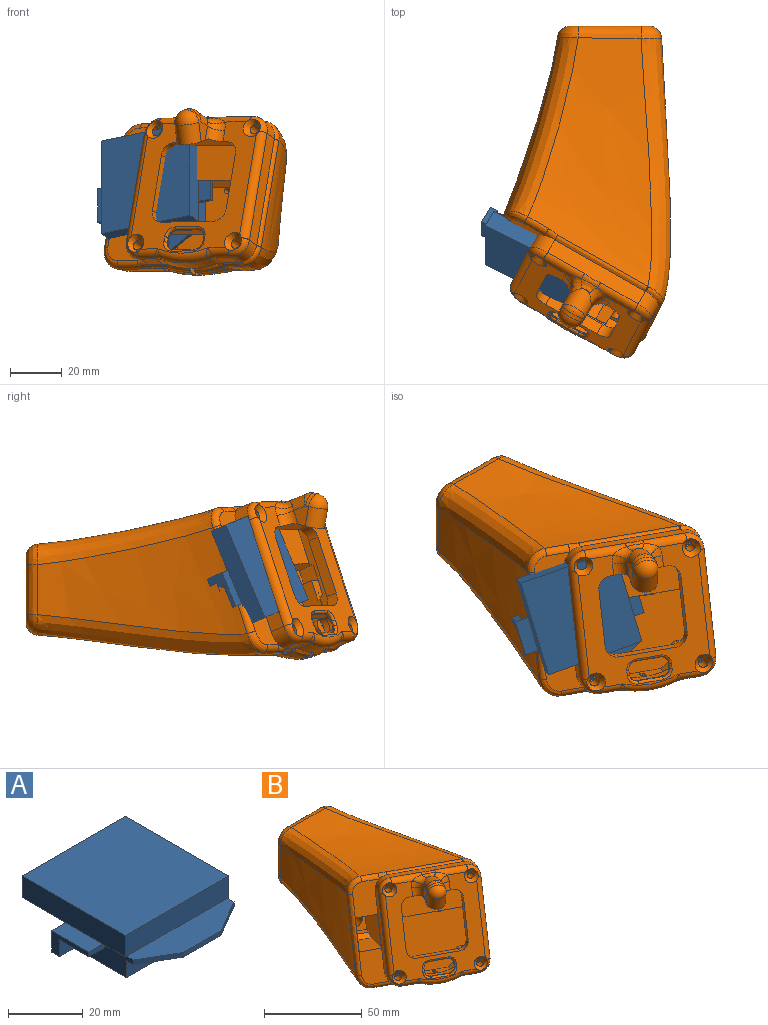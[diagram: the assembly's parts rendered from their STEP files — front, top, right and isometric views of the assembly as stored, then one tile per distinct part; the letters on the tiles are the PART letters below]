
ASSEMBLY  parts=2 mates=1
PART A: 32 faces, bbox 49.5x48.5x14 mm
  f0: plane 14x7mm, normal (-1,0,0), area 37.5mm2, adj f1,f7,f10,f13,f30,f31
  f1: plane 5.75x1.5mm, normal (0,-1,0), area 8.6mm2, adj f0,f11,f13,f14,f31
  f2: plane 5.75x1.5mm, normal (0,-1,0), area 8.6mm2, adj f3,f8,f12,f15,f29
  f3: plane 14x7mm, normal (1,0,0), area 37.5mm2, adj f2,f7,f8,f10,f28,f29
  f4: plane 12x7mm, normal (-0.5,-0.86,0), area 20.8mm2, adj f5,f9,f11,f27
  f5: plane 14x1.5mm, normal (0,-1,0), area 21mm2, adj f4,f6,f9,f27
  f6: plane 12x7mm, normal (0.5,-0.86,0), area 20.8mm2, adj f5,f9,f12,f27
  f7: plane 49.5x22.5mm, normal (0,0,-1), area 802.5mm2, adj f0,f3,f10,f11,f12,f22,f23,f24
  f8: plane 14x5.25mm, normal (0,0,1), area 73.5mm2, adj f2,f3,f10,f19
  f9: plane 38x9.5mm, normal (0,0,1), area 277mm2, adj f4,f5,f6,f11,f12,f18
  f10: plane 49.5x7mm, normal (0,1,0), area 107.3mm2, adj f0,f3,f7,f8,f13,f21,f22,f23
  f11: plane 22x7mm, normal (-1,0,0), area 123.8mm2, adj f1,f4,f7,f9,f14,f26,f27,f30
  f12: plane 22x7mm, normal (1,0,0), area 123.8mm2, adj f2,f6,f7,f9,f15,f26,f27,f28
  f13: plane 14x5.25mm, normal (0,0,1), area 73.5mm2, adj f0,f1,f10,f17
  f14: plane 8.5x0.5mm, normal (0,0,-1), area 4.2mm2, adj f1,f11,f17,f18
  f15: plane 8.5x0.5mm, normal (0,0,-1), area 4.3mm2, adj f2,f12,f18,f19
  f16: plane 39x7mm, normal (0,1,0), area 273mm2, adj f17,f19,f20,f21
  f17: plane 39x7mm, normal (-1,0,0), area 273mm2, adj f13,f14,f16,f18,f20,f21
  f18: plane 39x7mm, normal (0,-1,0), area 273mm2, adj f9,f14,f15,f17,f19,f20
  f19: plane 39x7mm, normal (1,0,0), area 273mm2, adj f8,f15,f16,f18,f20,f21
  f20: plane 39x39mm, normal (0,0,1), area 1521mm2, adj f16,f17,f18,f19
  f21: plane 39x16.5mm, normal (0,0,-1), area 643.5mm2, adj f10,f16,f17,f19
  f22: plane 5.5x2mm, normal (1,0,0), area 11mm2, adj f7,f10,f24,f25
  f23: plane 5.5x2mm, normal (-1,0,0), area 11mm2, adj f7,f10,f24,f25
  f24: plane 43.5x5.5mm, normal (0,1,0), area 239.2mm2, adj f7,f22,f23,f25
  f25: plane 43.5x2mm, normal (0,0,-1), area 87mm2, adj f10,f22,f23,f24
  f26: plane 38x5.5mm, normal (0,-1,0), area 209mm2, adj f7,f11,f12,f27
  f27: plane 38x9.5mm, normal (0,0,-1), area 277mm2, adj f4,f5,f6,f11,f12,f26
  f28: plane 5.75x5.5mm, normal (0,-1,0), area 31.6mm2, adj f3,f7,f12,f29
  f29: plane 11x5.75mm, normal (0,0,-1), area 63.2mm2, adj f2,f3,f12,f28
  f30: plane 5.75x5.5mm, normal (0,-1,0), area 31.6mm2, adj f0,f7,f11,f31
  f31: plane 11x5.75mm, normal (0,0,-1), area 63.2mm2, adj f0,f1,f11,f30
PART B: 314 faces, bbox 89.2x132.2x70.9 mm
  f0: cylinder r=2.3mm len=4.98mm, axis (-0.12,-0.17,0.98), area 36.2mm2, adj f1,f102,f306,f307
  f1: torus R=3mm, axis (-0.87,0.49,-0.02), area 47.5mm2, adj f0,f105,f308,f309
  f2: plane 39.21x38.23mm, normal (0.47,0.81,-0.34), area 1463.8mm2, adj f129,f130,f151,f152,f153,f154,f278,f279
  f3: plane 1.48x1.13mm, normal (0.47,0.81,-0.34), area 0.5mm2, adj f12,f96,f289
  f4: plane 1.62x0.92mm, normal (0.47,0.81,-0.34), area 0.5mm2, adj f12,f39,f288
  f5: plane 1.88x1.74mm, normal (0.47,0.81,-0.34), area 0.9mm2, adj f38,f39,f295
  f6: plane 2.05x1.91mm, normal (0.47,0.81,-0.34), area 0.9mm2, adj f38,f96,f297
  f7: plane 1.62x0.92mm, normal (0.47,0.81,-0.34), area 0.5mm2, adj f11,f96,f292
  f8: plane 1.88x1.74mm, normal (0.47,0.81,-0.34), area 0.9mm2, adj f36,f96,f300
  f9: plane 2.05x1.91mm, normal (0.47,0.81,-0.34), area 0.9mm2, adj f36,f37,f302
  f10: plane 1.48x1.13mm, normal (0.47,0.81,-0.34), area 0.5mm2, adj f11,f37,f291
  f11: plane 37.28x15.33mm, normal (-0.87,0.49,-0.02), area 156mm2, adj f7,f10,f14,f94,f98,f99,f100,f291
  f12: plane 37.28x15.33mm, normal (0.87,-0.49,0.02), area 156mm2, adj f3,f4,f14,f94,f97,f99,f100,f288
  f13: plane 34.01x20.01mm, normal (0.47,0.81,-0.34), area 67.8mm2, adj f14,f40,f41,f42,f43,f95,f164,f241
  f14: plane 36.22x23.14mm, normal (0.16,0.3,0.94), area 102.7mm2, adj f11,f12,f13,f15,f94,f97,f98,f266
  f15: plane 25.65x15.22mm, normal (0.47,0.81,-0.34), area 55.8mm2, adj f14,f248,f263,f264,f265,f266,f267,f268
  f16: plane 2.37x1.14mm, normal (-0.47,-0.81,0.34), area 0.3mm2, adj f244,f245,f264
  f17: plane 2.2x1.46mm, normal (-0.47,-0.81,0.34), area 0.3mm2, adj f244,f249,f264
  f18: plane 8.05x7.05mm, normal (0.47,0.81,-0.34), area 34.6mm2, adj f248,f249,f250,f251,f264,f265
  f19: plane 7.15x7.09mm, normal (0.47,0.81,-0.34), area 34.6mm2, adj f245,f246,f247,f248,f263,f264
  f20: cylinder r=40mm len=12.67mm, axis (-0.47,-0.81,0.34), area 31.5mm2, adj f21,f181,f182,f242
  f21: bspline ~10.64x5.97mm, area 26.4mm2, adj f20,f164,f196,f242,f274
  f22: cone r=0mm half-angle=59deg, axis (-0.47,-0.81,0.34), area 6.8mm2, adj f177,f240
  f23: cone r=0mm half-angle=59deg, axis (-0.47,-0.81,0.34), area 6.8mm2, adj f175,f238
  f24: cone r=0mm half-angle=59deg, axis (-0.47,-0.81,0.34), area 6.8mm2, adj f173,f236
  f25: cone r=0mm half-angle=59deg, axis (-0.47,-0.81,0.34), area 6.8mm2, adj f171,f234
  f26: plane 51.05x48.58mm, normal (-0.47,-0.81,0.34), area 1023.4mm2, adj f27,f28,f29,f30,f31,f32,f90,f91
  f27: cylinder r=3mm len=42.42mm, axis (0.16,0.3,0.94), area 206.1mm2, adj f26,f86,f165,f167,f172,f178
  f28: cylinder r=3mm len=16.24mm, axis (0.87,-0.49,0.02), area 70.2mm2, adj f26,f89,f167,f169,f178,f228
  f29: cylinder r=3mm len=42.32mm, axis (-0.16,-0.3,-0.94), area 206.1mm2, adj f26,f88,f168,f170,f174,f176
  f30: cylinder r=3mm len=16.5mm, axis (0.87,-0.49,0.02), area 71.6mm2, adj f26,f89,f169,f170,f176,f230
  f31: cylinder r=3mm len=9.07mm, axis (-0.87,0.49,-0.02), area 38mm2, adj f26,f33,f168,f174,f275
  f32: cylinder r=3mm len=8.81mm, axis (-0.87,0.49,-0.02), area 36.6mm2, adj f26,f87,f165,f172,f277
  f33: plane 9.02x8.41mm, normal (-0.16,-0.3,-0.94), area 42.8mm2, adj f31,f156,f190,f192,f194,f274
  f34: plane 51.68x22.7mm, normal (-0.47,-0.81,0.34), area 442.6mm2, adj f44,f46,f47,f48,f86,f155,f158,f199
  f35: plane 44.3x31.36mm, normal (-0.47,-0.81,0.34), area 1192.8mm2, adj f36,f38,f40,f41,f42,f43,f95,f96
  f36: plane 14.13x10.96mm, normal (-0.87,0.49,-0.02), area 62.4mm2, adj f8,f9,f35,f37,f96,f148,f149,f301
  f37: plane 5.43x3.75mm, normal (0.16,0.3,0.94), area 6.7mm2, adj f9,f10,f36,f41,f98,f149,f303
  f38: plane 14.13x10.96mm, normal (0.87,-0.49,0.02), area 62.4mm2, adj f5,f6,f35,f39,f96,f143,f145,f296
  f39: plane 5.43x3.75mm, normal (0.16,0.3,0.94), area 6.7mm2, adj f4,f5,f38,f43,f97,f145,f294
  f40: plane 11.47x9.97mm, normal (-0.33,0.52,0.79), area 67.8mm2, adj f13,f35,f41,f95,f137,f141
  f41: plane 18.04x12.36mm, normal (-0.87,0.49,-0.02), area 123.4mm2, adj f13,f35,f37,f40,f98,f138,f141,f148
  f42: plane 12.49x10.94mm, normal (0.59,0,0.81), area 67.8mm2, adj f13,f35,f43,f95,f131,f135
  f43: plane 18.04x12.36mm, normal (0.87,-0.49,0.02), area 123.4mm2, adj f13,f35,f39,f42,f97,f133,f135,f143
  f44: plane 23.33x20.35mm, normal (0.16,0.3,0.94), area 253.7mm2, adj f34,f46,f47,f127
  f45: plane 12.88x12.36mm, normal (-0.47,-0.81,0.34), area 95.7mm2, adj f46,f47,f111,f125,f128
  f46: plane 29.25x25.15mm, normal (0.87,-0.49,0.02), area 513.1mm2, adj f34,f44,f45,f48,f125,f126,f127,f128
  f47: plane 29.25x25.15mm, normal (-0.87,0.49,-0.02), area 513.1mm2, adj f34,f44,f45,f48,f125,f126,f127,f128
  f48: plane 23.33x20.35mm, normal (-0.16,-0.3,-0.94), area 253.7mm2, adj f34,f46,f47,f126
  f49: plane 11x8.5mm, normal (0,1,0), area 39.4mm2, adj f50,f82,f84,f123,f124
  f50: cylinder r=4.15mm len=8.3mm, axis (0,1,0), area 109.3mm2, adj f49,f55,f313
  f51: plane 32.12x2.88mm, normal (0.57,0,0.82), area 106.5mm2, adj f53,f57,f115,f284,f312
  f52: plane 39.5x39.45mm, normal (0,0,-1), area 982.6mm2, adj f53,f56,f58,f116,f122,f278,f280,f287
  f53: plane 30.04x6.13mm, normal (1,0,0), area 172.5mm2, adj f51,f52,f280,f282,f284,f312
  f54: bspline ~46.34x45.04mm, area 1291.2mm2, adj f55,f116,f119,f120,f279,f287,f304
  f55: plane 17.61x17.4mm, normal (-0.17,-0.98,0), area 253.1mm2, adj f50,f54,f115,f117,f313
  f56: bspline ~30x26.65mm, area 34.9mm2, adj f52,f58,f278,f285
  f57: bspline ~44.17x31.12mm, area 519.2mm2, adj f51,f114,f115,f117,f118,f281,f283,f284
  f58: bspline ~40.13x38.49mm, area 722mm2, adj f52,f56,f285,f287
  f59: plane 7.87x5.82mm, normal (-0.87,0.49,-0.02), area 34.1mm2, adj f102,f106,f108,f110,f226
  f60: plane 30.55x25.51mm, normal (0,1,0), area 353.1mm2, adj f74,f75,f179,f208,f209,f210,f211,f212
  f61: bspline ~124.98x70.78mm, area 3534.6mm2, adj f160,f161,f180,f182,f183,f184,f185,f192
  f62: plane 18.13x15.13mm, normal (0,0,1), area 239.7mm2, adj f69,f72,f73,f74,f75,f76,f179,f220
  f63: bspline ~90.35x62.26mm, area 2378.1mm2, adj f161,f162,f203,f214
  f64: bspline ~124.98x63.62mm, area 3405.4mm2, adj f159,f160,f187,f189,f210
  f65: bspline ~106.69x69.6mm, area 3144.9mm2, adj f159,f162,f195,f197,f199,f212
  f66: plane 18.04x10.34mm, normal (1,0,0), area 185.4mm2, adj f69,f70,f73,f179
  f67: plane 18.02x15.02mm, normal (0,0,-1), area 270mm2, adj f69,f70,f71,f179
  f68: plane 18.04x10.34mm, normal (-1,0,0), area 185.4mm2, adj f69,f71,f72,f179
  f69: plane 29x24.3mm, normal (0,1,0), area 596.6mm2, adj f62,f66,f67,f68,f70,f71,f72,f73
  f70: cylinder r=7mm len=18mm, axis (0,1,0), area 197.9mm2, adj f66,f67,f69,f179
  f71: cylinder r=7mm len=18mm, axis (0,-1,0), area 197.9mm2, adj f67,f68,f69,f179
  f72: cylinder r=7mm len=18mm, axis (0,1,0), area 197.9mm2, adj f62,f68,f69,f179
  f73: cylinder r=7mm len=18mm, axis (0,-1,0), area 197.9mm2, adj f62,f66,f69,f179
  f74: plane 10.05x5.77mm, normal (-1,0,0), area 37.3mm2, adj f60,f62,f179,f208,f219,f220
  f75: plane 10.14x5.93mm, normal (1,0,0), area 37.6mm2, adj f60,f62,f179,f216,f217,f223
  f76: plane 3.34x0.54mm, normal (0,1,0), area 1.7mm2, adj f62,f218,f220,f221,f223,f224
  f77: plane 12.7x2.8mm, normal (0,0,-1), area 35.6mm2, adj f69,f78,f80,f81
  f78: plane 5.2x2.8mm, normal (1,0,0), area 14.6mm2, adj f69,f77,f79,f81
  f79: plane 12.7x2.8mm, normal (0,0,1), area 35.6mm2, adj f69,f78,f80,f81
  f80: plane 5.2x2.8mm, normal (-1,0,0), area 14.6mm2, adj f69,f77,f79,f81
  f81: plane 16x8.5mm, normal (0,-1,0), area 70mm2, adj f77,f78,f79,f80,f82,f83,f84,f85
  f82: plane 29.7x16mm, normal (0,0,1), area 454.7mm2, adj f49,f81,f83,f85,f123,f124
  f83: plane 21.5x8.5mm, normal (-1,0,0), area 182.8mm2, adj f81,f82,f84,f124
  f84: plane 29.7x16mm, normal (0,0,-1), area 454.7mm2, adj f49,f81,f83,f85,f123,f124
  f85: plane 21.5x8.5mm, normal (1,0,0), area 182.8mm2, adj f81,f82,f84,f123
  f86: plane 43.39x18.3mm, normal (-0.87,0.49,-0.02), area 264mm2, adj f27,f34,f155,f158
  f87: plane 8.76x8.26mm, normal (-0.16,-0.3,-0.94), area 41mm2, adj f32,f155,f202,f204,f276
  f88: plane 43.39x18.3mm, normal (0.87,-0.49,0.02), area 264mm2, adj f29,f156,f157,f186,f187
  f89: plane 38.01x24.92mm, normal (0.16,0.3,0.94), area 244.4mm2, adj f28,f30,f157,f158,f169,f193,f195
  f90: plane 23.11x10.59mm, normal (-0.87,0.49,-0.02), area 101.2mm2, adj f26,f94,f269,f272
  f91: plane 22.05x14.96mm, normal (0.16,0.3,0.94), area 101.2mm2, adj f26,f94,f269,f270
  f92: plane 23.11x10.59mm, normal (0.87,-0.49,0.02), area 101.2mm2, adj f26,f94,f270,f271
  f93: plane 22.05x14.96mm, normal (-0.16,-0.3,-0.94), area 143.5mm2, adj f26,f94,f102,f226,f232,f271,f272
  f94: plane 39.98x36.35mm, normal (0.47,0.81,-0.34), area 422.1mm2, adj f11,f12,f14,f90,f91,f92,f93,f100
  f95: plane 17.66x14.43mm, normal (0.16,0.3,0.94), area 116.2mm2, adj f13,f35,f40,f42,f241,f242,f243,f260
  f96: plane 47.03x31.15mm, normal (-0.16,-0.3,-0.94), area 398.4mm2, adj f3,f6,f7,f8,f35,f36,f38,f99
  f97: plane 7.71x2.65mm, normal (-0.47,-0.81,0.34), area 2.5mm2, adj f12,f14,f39,f43
  f98: plane 7.71x2.65mm, normal (-0.47,-0.81,0.34), area 2.5mm2, adj f11,f14,f37,f41
  f99: plane 36.43x24.03mm, normal (-0.47,-0.81,0.34), area 595.8mm2, adj f11,f12,f96,f100
  f100: plane 36.22x23.14mm, normal (-0.16,-0.3,-0.94), area 180.3mm2, adj f11,f12,f94,f99
  f101: plane 7.87x5.82mm, normal (0.87,-0.49,0.02), area 34.1mm2, adj f102,f106,f108,f110,f232
  f102: plane 12.21x12.17mm, normal (0.12,0.17,-0.98), area 74.9mm2, adj f0,f59,f93,f101,f110,f226,f232,f306
  f103: cylinder r=2.3mm len=6.68mm, axis (0.47,0.81,-0.34), area 71.2mm2, adj f104,f129
  f104: cylinder r=2.3mm len=8.33mm, axis (0.49,0.87,-0.07), area 95.7mm2, adj f103,f105
  f105: cylinder r=2.3mm len=7.01mm, axis (0.47,0.81,-0.34), area 72mm2, adj f1,f104,f310
  f106: cylinder r=5mm len=12.56mm, axis (-0.47,-0.81,0.34), area 107.4mm2, adj f59,f101,f107,f227,f228,f229,f230,f231
  f107: sphere r=5mm, area 27.9mm2, adj f106,f108
  f108: cylinder r=5mm len=9.46mm, axis (-0.48,-0.85,-0.21), area 23.8mm2, adj f59,f101,f107,f109
  f109: sphere r=5mm, area 314.2mm2, adj f108,f110
  f110: cylinder r=5mm len=10.21mm, axis (0.12,0.17,-0.98), area 121.3mm2, adj f59,f101,f102,f109
  f111: cylinder r=4.5mm len=15mm, axis (-0.47,-0.81,0.34), area 339.3mm2, adj f45,f112,f273
  f112: plane 8.47x7.93mm, normal (-0.47,-0.81,0.34), area 6.8mm2, adj f111,f273
  f113: torus R=7mm, axis (0.07,-0.42,-0.9), area 112.2mm2, adj f118,f273
  f114: bspline ~47.44x39.06mm, area 1173.6mm2, adj f57,f119,f281,f304
  f115: plane 39.42x36.15mm, normal (0,0,1), area 916.5mm2, adj f51,f55,f57,f116,f122,f312,f313
  f116: plane 33.11x8.91mm, normal (-1,0,0), area 216.9mm2, adj f52,f54,f115,f122,f287
  f117: plane 34.01x33.62mm, normal (0,0,-1), area 731.1mm2, adj f55,f57,f118,f120,f121,f311,f313
  f118: plane 13.53x9mm, normal (0.99,0,0.1), area 95.2mm2, adj f57,f113,f117,f119,f311
  f119: plane 56.67x30.91mm, normal (0,0,1), area 647.1mm2, adj f54,f114,f118,f120,f121,f304,f311
  f120: plane 26.52x9.02mm, normal (-1,0,0), area 238.4mm2, adj f54,f117,f119,f121
  f121: plane 17.27x9mm, normal (0,-1,0), area 151.2mm2, adj f117,f119,f120,f311
  f122: plane 17x8mm, normal (0,-1,0), area 136mm2, adj f52,f115,f116,f312
  f123: plane 8.5x8.2mm, normal (0.96,0.29,0), area 72.9mm2, adj f49,f82,f84,f85
  f124: plane 8.5x8.2mm, normal (-0.96,0.29,0), area 72.9mm2, adj f49,f82,f83,f84
  f125: plane 12.84x10.31mm, normal (-0.16,-0.3,-0.94), area 64.9mm2, adj f45,f46,f47,f126
  f126: plane 11.3x7.56mm, normal (-0.41,-0.74,-0.53), area 45mm2, adj f46,f47,f48,f125
  f127: plane 12.03x9mm, normal (-0.17,-0.26,0.95), area 45mm2, adj f44,f46,f47,f128
  f128: plane 12.84x10.31mm, normal (0.16,0.3,0.94), area 64.9mm2, adj f45,f46,f47,f127
  f129: bspline ~13.08x12.48mm, area 230.8mm2, adj f2,f103,f130,f285
  f130: cylinder r=4mm len=8.02mm, axis (-0.22,-0.36,0.91), area 27.7mm2, adj f2,f129
  f131: plane 5.54x4.69mm, normal (0.66,-0.58,-0.48), area 17.2mm2, adj f35,f42,f132,f135
  f132: cylinder r=2.53mm len=7.78mm, axis (0.47,0.81,-0.34), area 36.6mm2, adj f35,f131,f133,f135
  f133: plane 7.51x6.67mm, normal (0.16,0.3,0.94), area 27.2mm2, adj f35,f43,f132,f135
  f134: cylinder r=0.25mm len=5.82mm, axis (0.47,0.81,-0.34), area 10.7mm2, adj f135,f136
  f135: plane 5.79x5.64mm, normal (-0.47,-0.81,0.34), area 28.1mm2, adj f42,f43,f131,f132,f133,f134
  f136: plane 0.47x0.44mm, normal (-0.47,-0.81,0.34), area 0.2mm2, adj f134
  f137: plane 6.85x4.33mm, normal (-0.82,0.26,-0.51), area 17.2mm2, adj f35,f40,f140,f141
  f138: plane 7.51x6.67mm, normal (0.16,0.3,0.94), area 27.2mm2, adj f35,f41,f140,f141
  f139: cylinder r=0.25mm len=5.82mm, axis (0.47,0.81,-0.34), area 10.7mm2, adj f141,f142
  f140: cylinder r=2.53mm len=6.35mm, axis (0.47,0.81,-0.34), area 36.6mm2, adj f35,f137,f138,f141
  f141: plane 6.1x5.73mm, normal (-0.47,-0.81,0.34), area 28.1mm2, adj f40,f41,f137,f138,f139,f140
  f142: plane 0.47x0.44mm, normal (-0.47,-0.81,0.34), area 0.2mm2, adj f139
  f143: plane 8.3x8.06mm, normal (0.16,0.3,0.94), area 38.1mm2, adj f35,f38,f43,f145
  f144: cylinder r=0.25mm len=5.82mm, axis (0.47,0.81,-0.34), area 10.7mm2, adj f145,f146
  f145: plane 7.61x6.11mm, normal (-0.47,-0.81,0.34), area 44.6mm2, adj f38,f39,f43,f143,f144
  f146: plane 0.47x0.44mm, normal (-0.47,-0.81,0.34), area 0.2mm2, adj f144
  f147: cylinder r=0.25mm len=5.82mm, axis (0.47,0.81,-0.34), area 10.7mm2, adj f149,f150
  f148: plane 8.3x8.06mm, normal (0.16,0.3,0.94), area 38.1mm2, adj f35,f36,f41,f149
  f149: plane 7.61x6.11mm, normal (-0.47,-0.81,0.34), area 44.6mm2, adj f36,f37,f41,f147,f148
  f150: plane 0.47x0.44mm, normal (-0.47,-0.81,0.34), area 0.2mm2, adj f147
  f151: plane 4.45x4.17mm, normal (-0.16,-0.3,-0.94), area 10.5mm2, adj f2,f35,f152,f154
  f152: cylinder r=1.1mm len=3.42mm, axis (-0.47,-0.81,0.34), area 10.4mm2, adj f2,f35,f151,f153
  f153: plane 4.45x4.17mm, normal (0.16,0.3,0.94), area 10.5mm2, adj f2,f35,f152,f154
  f154: cylinder r=1.1mm len=3.42mm, axis (-0.47,-0.81,0.34), area 10.4mm2, adj f2,f35,f151,f153
  f155: cylinder r=7mm len=10.48mm, axis (0.47,0.81,-0.34), area 66mm2, adj f34,f86,f87,f165,f206
  f156: cylinder r=7mm len=9.99mm, axis (-0.47,-0.81,0.34), area 66mm2, adj f33,f88,f168,f188
  f157: cylinder r=7mm len=10.48mm, axis (0.47,0.81,-0.34), area 66mm2, adj f88,f89,f170,f189,f191
  f158: cylinder r=7mm len=9.99mm, axis (-0.47,-0.81,0.34), area 66mm2, adj f34,f86,f89,f167,f197
  f159: bspline ~104.06x23.48mm, area 1291.4mm2, adj f64,f65,f191,f193,f211
  f160: bspline ~120.13x15.62mm, area 1388.5mm2, adj f61,f64,f186,f188,f190,f209
  f161: bspline ~90.11x36.21mm, area 1133.4mm2, adj f61,f63,f205,f215
  f162: bspline ~72.35x28.38mm, area 903.5mm2, adj f63,f65,f201,f213
  f163: cylinder r=40mm len=11.95mm, axis (-0.47,-0.81,0.34), area 30.7mm2, adj f181,f184,f198,f241
  f164: cylinder r=35mm len=20.75mm, axis (-0.47,-0.81,0.34), area 125.7mm2, adj f13,f21,f166,f198,f274,f276
  f165: torus R=4mm, axis (-0.47,-0.81,0.34), area 32.9mm2, adj f27,f32,f155,f172
  f166: torus R=32mm, axis (-0.47,-0.81,0.34), area 104.5mm2, adj f26,f164,f275,f277
  f167: torus R=4mm, axis (-0.47,-0.81,0.34), area 32.9mm2, adj f27,f28,f158,f178
  f168: torus R=4mm, axis (-0.47,-0.81,0.34), area 33mm2, adj f29,f31,f156,f174
  f169: bspline ~8.98x7.36mm, area 12.8mm2, adj f28,f30,f89,f229
  f170: torus R=4mm, axis (-0.47,-0.81,0.34), area 33mm2, adj f29,f30,f157,f176
  f171: cylinder r=1.95mm len=7.86mm, axis (-0.47,-0.81,0.34), area 84.2mm2, adj f25,f172
  f172: cone r=1.95mm half-angle=41deg, axis (-0.47,-0.81,0.34), area 48.9mm2, adj f26,f27,f32,f165,f171
  f173: cylinder r=1.95mm len=7.86mm, axis (-0.47,-0.81,0.34), area 84.2mm2, adj f24,f174
  f174: cone r=1.95mm half-angle=41deg, axis (-0.47,-0.81,0.34), area 47.8mm2, adj f26,f29,f31,f168,f173
  f175: cylinder r=1.95mm len=7.86mm, axis (-0.47,-0.81,0.34), area 84.2mm2, adj f23,f176
  f176: cone r=1.95mm half-angle=41deg, axis (-0.47,-0.81,0.34), area 47.8mm2, adj f26,f29,f30,f170,f175
  f177: cylinder r=1.95mm len=7.86mm, axis (-0.47,-0.81,0.34), area 84.2mm2, adj f22,f178
  f178: cone r=1.95mm half-angle=41deg, axis (-0.47,-0.81,0.34), area 48.9mm2, adj f26,f27,f28,f167,f177
  f179: bspline ~29x24.3mm, area 562.1mm2, adj f60,f62,f66,f67,f68,f70,f71,f72
  f180: bspline ~37.91x24.25mm, area 63.3mm2, adj f61,f181
  f181: bspline ~33.74x20.62mm, area 174.6mm2, adj f20,f163,f180,f183,f185,f241,f242,f243
  f182: bspline ~6.06x5.04mm, area 6.9mm2, adj f20,f61,f183,f194,f196
  f183: bspline ~6.69x6.43mm, area 6.4mm2, adj f61,f181,f182
  f184: bspline ~6.06x2.58mm, area 6.6mm2, adj f61,f163,f185,f200,f202
  f185: bspline ~7.23x3.08mm, area 6.3mm2, adj f61,f181,f184
  f186: bspline ~1.86x1.51mm, area 0.2mm2, adj f88,f160,f187,f188
  f187: bspline ~58.67x20.21mm, area 108.4mm2, adj f64,f88,f186,f189
  f188: bspline ~10.4x8.75mm, area 29.4mm2, adj f156,f160,f186,f190
  f189: bspline ~1.91x1.68mm, area 0mm2, adj f64,f157,f187,f191
  f190: bspline ~1.57x1.54mm, area 0.3mm2, adj f33,f160,f188,f192
  f191: bspline ~9.56x8.32mm, area 28.7mm2, adj f157,f159,f189,f193
  f192: bspline ~6.45x4.67mm, area 15.6mm2, adj f33,f61,f190,f194
  f193: bspline ~2.43x2.21mm, area 0.8mm2, adj f89,f159,f191,f195
  f194: bspline ~3.02x2.3mm, area 4.7mm2, adj f33,f182,f192,f196,f274
  f195: bspline ~51.76x30.76mm, area 91.7mm2, adj f65,f89,f193,f197
  f196: bspline ~2.07x1.8mm, area 0.3mm2, adj f21,f182,f194,f274
  f197: bspline ~5.79x4.98mm, area 12mm2, adj f65,f158,f195,f199
  f198: bspline ~9.73x7.41mm, area 26.5mm2, adj f163,f164,f200,f241,f276
  f199: bspline ~35.17x21.89mm, area 35.7mm2, adj f34,f65,f197,f201
  f200: bspline ~2.52x2.3mm, area 0.2mm2, adj f184,f198,f202,f276
  f201: bspline ~10.88x10.06mm, area 41.8mm2, adj f34,f162,f199,f203
  f202: bspline ~2.76x2.44mm, area 4.9mm2, adj f87,f184,f200,f204,f276
  f203: bspline ~68.09x24.97mm, area 166.2mm2, adj f34,f63,f201,f205
  f204: bspline ~6.23x4.56mm, area 15.1mm2, adj f61,f87,f202,f206
  f205: bspline ~10.13x9.74mm, area 46.6mm2, adj f34,f161,f203,f207
  f206: bspline ~6x5.03mm, area 14.2mm2, adj f61,f155,f204,f207
  f207: bspline ~26.91x17.01mm, area 38.4mm2, adj f34,f61,f205,f206
  f208: bspline ~28.98x5.04mm, area 62.3mm2, adj f60,f61,f74,f209,f219
  f209: bspline ~9.77x9.76mm, area 73.8mm2, adj f60,f160,f208,f210
  f210: bspline ~40.56x5.12mm, area 149.3mm2, adj f60,f64,f209,f211
  f211: bspline ~9.81x9.76mm, area 73.1mm2, adj f60,f159,f210,f212
  f212: bspline ~43.6x5.11mm, area 184.5mm2, adj f60,f65,f211,f213
  f213: bspline ~9.79x9.75mm, area 68.9mm2, adj f60,f162,f212,f214
  f214: bspline ~27.08x4.98mm, area 141.3mm2, adj f60,f63,f213,f215
  f215: bspline ~9.78x8.43mm, area 69mm2, adj f60,f161,f214,f216
  f216: bspline ~28.99x5.06mm, area 64mm2, adj f60,f61,f75,f215,f217
  f217: bspline ~19.5x4.45mm, area 45.5mm2, adj f61,f75,f216,f224,f225
  f218: bspline ~24.54x3.25mm, area 20.9mm2, adj f61,f76,f222,f225
  f219: bspline ~19.51x4.32mm, area 45.6mm2, adj f61,f74,f208,f221,f222
  f220: cylinder r=2.5mm len=2.82mm, axis (0,0,-1), area 11.1mm2, adj f62,f74,f76,f221
  f221: bspline ~2.58x2.54mm, area 1.4mm2, adj f76,f219,f220,f222
  f222: bspline ~5.53x5.22mm, area 8.1mm2, adj f218,f219,f221
  f223: cylinder r=2.5mm len=2.89mm, axis (0,0,1), area 11.3mm2, adj f62,f75,f76,f224
  f224: bspline ~2.59x2.51mm, area 1.3mm2, adj f76,f217,f223,f225
  f225: bspline ~5.47x5.19mm, area 8.1mm2, adj f217,f218,f224
  f226: cylinder r=5mm len=8.26mm, axis (-0.16,-0.3,-0.94), area 36.4mm2, adj f26,f59,f93,f102,f227
  f227: torus R=10mm, axis (-0.47,-0.81,0.34), area 19.1mm2, adj f26,f106,f226,f228
  f228: bspline ~6.95x6.64mm, area 28mm2, adj f28,f106,f227,f229
  f229: bspline ~6.44x5.76mm, area 17.9mm2, adj f106,f169,f228,f230
  f230: bspline ~7.99x7.28mm, area 28mm2, adj f30,f106,f229,f231
  f231: torus R=10mm, axis (-0.47,-0.81,0.34), area 19.1mm2, adj f26,f106,f230,f232
  f232: cylinder r=5mm len=7.57mm, axis (0.16,0.3,0.94), area 36.4mm2, adj f26,f93,f101,f102,f231
  f233: cone r=0mm half-angle=59deg, axis (-0.47,-0.81,0.34), area 7.2mm2, adj f234
  f234: cylinder r=1.4mm len=9.9mm, axis (-0.47,-0.81,0.34), area 89.5mm2, adj f25,f233
  f235: cone r=0mm half-angle=59deg, axis (-0.47,-0.81,0.34), area 7.2mm2, adj f236
  f236: cylinder r=1.4mm len=9.9mm, axis (-0.47,-0.81,0.34), area 89.5mm2, adj f24,f235
  f237: cone r=0mm half-angle=59deg, axis (-0.47,-0.81,0.34), area 7.2mm2, adj f238
  f238: cylinder r=1.4mm len=9.9mm, axis (-0.47,-0.81,0.34), area 89.5mm2, adj f23,f237
  f239: cone r=0mm half-angle=59deg, axis (-0.47,-0.81,0.34), area 7.2mm2, adj f240
  f240: cylinder r=1.4mm len=9.9mm, axis (-0.47,-0.81,0.34), area 89.5mm2, adj f22,f239
  f241: plane 5.92x5.4mm, normal (0.87,-0.49,0.02), area 23.1mm2, adj f13,f95,f163,f181,f198,f261
  f242: plane 5.92x5.4mm, normal (-0.87,0.49,-0.02), area 23.1mm2, adj f13,f20,f21,f95,f181,f260
  f243: plane 3.93x1.57mm, normal (-0.47,-0.81,0.34), area 2.5mm2, adj f95,f181,f260,f261
  f244: plane 8.92x5.35mm, normal (0.16,0.3,0.94), area 5mm2, adj f16,f17,f245,f249,f256,f262
  f245: cylinder r=3mm len=3.31mm, axis (-0.47,-0.81,0.34), area 2.4mm2, adj f16,f19,f244,f246,f254
  f246: plane 2.05x1.02mm, normal (-0.87,0.49,-0.02), area 1mm2, adj f19,f245,f247,f252
  f247: cylinder r=3mm len=2.94mm, axis (-0.47,-0.81,0.34), area 2.4mm2, adj f19,f246,f248,f253
  f248: plane 20.84x14.27mm, normal (-0.16,-0.3,-0.94), area 100mm2, adj f15,f18,f19,f247,f250,f255,f263,f265
  f249: cylinder r=3mm len=2.94mm, axis (-0.47,-0.81,0.34), area 2.4mm2, adj f17,f18,f244,f251,f258
  f250: cylinder r=3mm len=3.31mm, axis (-0.47,-0.81,0.34), area 2.4mm2, adj f18,f248,f251,f257
  f251: plane 2.05x1.02mm, normal (0.87,-0.49,0.02), area 1mm2, adj f18,f249,f250,f259
  f252: cylinder r=1mm len=2.24mm, axis (-0.16,-0.3,-0.94), area 3.1mm2, adj f26,f246,f253,f254
  f253: torus R=4mm, axis (-0.47,-0.81,0.34), area 8.3mm2, adj f26,f247,f252,f255
  f254: torus R=4mm, axis (-0.47,-0.81,0.34), area 8.3mm2, adj f26,f245,f252,f256
  f255: cylinder r=1mm len=9.03mm, axis (0.87,-0.49,0.02), area 15.7mm2, adj f26,f248,f253,f257
  f256: cylinder r=1mm len=9.31mm, axis (-0.87,0.49,-0.02), area 15.7mm2, adj f26,f244,f254,f258
  f257: torus R=4mm, axis (-0.47,-0.81,0.34), area 8.3mm2, adj f26,f250,f255,f259
  f258: torus R=4mm, axis (-0.47,-0.81,0.34), area 8.3mm2, adj f26,f249,f256,f259
  f259: cylinder r=1mm len=2.21mm, axis (0.16,0.3,0.94), area 3.1mm2, adj f26,f251,f257,f258
  f260: cylinder r=0.7mm len=4.33mm, axis (0.16,0.3,0.94), area 4.7mm2, adj f95,f181,f242,f243
  f261: cylinder r=0.7mm len=4.31mm, axis (-0.16,-0.3,-0.94), area 4.7mm2, adj f95,f181,f241,f243
  f262: plane 7.07x4.03mm, normal (0.47,0.81,-0.34), area 1.6mm2, adj f244,f264
  f263: cylinder r=2.9mm len=6.66mm, axis (0.47,0.81,-0.34), area 34.3mm2, adj f15,f19,f248,f264
  f264: cylinder r=27.45mm len=23.05mm, axis (0.47,0.81,-0.34), area 110mm2, adj f15,f16,f17,f18,f19,f262,f263,f265
  f265: cylinder r=2.9mm len=6.7mm, axis (0.47,0.81,-0.34), area 34.3mm2, adj f15,f18,f248,f264
  f266: cylinder r=3.9mm len=7.64mm, axis (-0.47,-0.81,0.34), area 27mm2, adj f13,f14,f15,f268
  f267: cylinder r=3.9mm len=7.64mm, axis (-0.47,-0.81,0.34), area 27mm2, adj f13,f14,f15,f268
  f268: cylinder r=28.45mm len=23.21mm, axis (-0.47,-0.81,0.34), area 80.3mm2, adj f13,f15,f266,f267
  f269: cylinder r=5mm len=7.19mm, axis (-0.47,-0.81,0.34), area 34.6mm2, adj f26,f90,f91,f94
  f270: cylinder r=5mm len=7.58mm, axis (0.47,0.81,-0.34), area 34.6mm2, adj f26,f91,f92,f94
  f271: cylinder r=5mm len=7.19mm, axis (-0.47,-0.81,0.34), area 34.6mm2, adj f26,f92,f93,f94
  f272: cylinder r=5mm len=7.58mm, axis (0.47,0.81,-0.34), area 34.6mm2, adj f26,f90,f93,f94
  f273: bspline ~7.89x7.63mm, area 43.3mm2, adj f111,f112,f113
  f274: cylinder r=10mm len=6.27mm, axis (-0.47,-0.81,0.34), area 18.1mm2, adj f21,f33,f164,f194,f196,f275
  f275: bspline ~4.42x3.59mm, area 5.8mm2, adj f31,f166,f274
  f276: cylinder r=10mm len=6.55mm, axis (-0.47,-0.81,0.34), area 18.1mm2, adj f87,f164,f198,f200,f202,f277
  f277: bspline ~4.4x3.52mm, area 5.8mm2, adj f32,f166,f276
  f278: bspline ~18.83x8.31mm, area 14.3mm2, adj f2,f52,f56,f280,f285
  f279: bspline ~53.36x19.24mm, area 129.8mm2, adj f2,f54,f286,f305
  f280: cylinder r=2mm len=5.8mm, axis (-0.87,0.5,0), area 8.6mm2, adj f2,f52,f53,f278,f282
  f281: bspline ~47.25x28.26mm, area 125.7mm2, adj f2,f57,f114,f283,f305
  f282: cylinder r=2mm len=6.37mm, axis (0,-0.39,-0.92), area 10.1mm2, adj f2,f53,f280,f284
  f283: bspline ~46.1x17.23mm, area 94.1mm2, adj f2,f57,f281,f284
  f284: cylinder r=2mm len=4.42mm, axis (0.67,-0.58,-0.47), area 9.8mm2, adj f2,f51,f53,f57,f282,f283
  f285: bspline ~47.12x28.35mm, area 110mm2, adj f2,f56,f58,f129,f278,f286
  f286: sphere r=2mm, area 6.9mm2, adj f279,f285,f287
  f287: bspline ~36.44x8.27mm, area 88.7mm2, adj f52,f54,f58,f116,f286
  f288: cylinder r=2mm len=2.07mm, axis (0.47,0.81,-0.34), area 1mm2, adj f4,f12,f294
  f289: cylinder r=2mm len=1.9mm, axis (0.47,0.81,-0.34), area 1mm2, adj f3,f12,f298
  f290: plane 10.95x5.31mm, normal (0.47,0.81,-0.34), area 44mm2, adj f12,f294,f295,f296,f297,f298
  f291: cylinder r=2mm len=1.9mm, axis (0.47,0.81,-0.34), area 1mm2, adj f10,f11,f303
  f292: cylinder r=2mm len=2.07mm, axis (0.47,0.81,-0.34), area 1mm2, adj f7,f11,f299
  f293: plane 10.95x5.31mm, normal (0.47,0.81,-0.34), area 44mm2, adj f11,f299,f300,f301,f302,f303
  f294: plane 3.48x2.84mm, normal (0.44,0.79,0.42), area 6.3mm2, adj f12,f39,f288,f290,f295
  f295: cone r=2mm half-angle=45deg, axis (0.47,0.81,-0.34), area 4.2mm2, adj f5,f290,f294,f296
  f296: plane 10.5x5.19mm, normal (0.95,0.23,-0.23), area 22.5mm2, adj f38,f290,f295,f297
  f297: cone r=2mm half-angle=45deg, axis (0.47,0.81,-0.34), area 4.2mm2, adj f6,f290,f296,f298
  f298: plane 3.75x3.66mm, normal (0.22,0.36,-0.91), area 6.3mm2, adj f12,f96,f289,f290,f297
  f299: plane 4.25x3.12mm, normal (0.22,0.36,-0.91), area 6.3mm2, adj f11,f96,f292,f293,f300
  f300: cone r=2mm half-angle=45deg, axis (0.47,0.81,-0.34), area 4.2mm2, adj f8,f293,f299,f301
  f301: plane 10.45x3.71mm, normal (-0.28,0.93,-0.25), area 22.5mm2, adj f36,f293,f300,f302
  f302: cone r=2mm half-angle=45deg, axis (0.47,0.81,-0.34), area 4.2mm2, adj f9,f293,f301,f303
  f303: plane 3.78x2.4mm, normal (0.44,0.79,0.42), area 6.3mm2, adj f11,f37,f291,f293,f302
  f304: bspline ~47.95x8.8mm, area 182.7mm2, adj f54,f114,f119,f305
  f305: bspline ~5.79x5.14mm, area 17.7mm2, adj f2,f279,f281,f304
  f306: plane 3.98x3.14mm, normal (-0.4,0.91,0.11), area 10.6mm2, adj f0,f102,f307,f308
  f307: plane 3.92x3.54mm, normal (0.98,0.13,0.14), area 10.6mm2, adj f0,f102,f306,f309
  f308: cone r=6.78mm half-angle=52.5deg, axis (-0.87,0.49,-0.02), area 24.7mm2, adj f1,f306,f309,f310
  f309: cone r=4.4mm half-angle=52.5deg, axis (0.87,-0.49,0.02), area 24.7mm2, adj f1,f307,f308,f310
  f310: torus R=6mm, axis (0.87,-0.49,0.02), area 15mm2, adj f105,f308,f309
  f311: plane 12.69x9mm, normal (0.56,-0.83,0.06), area 128.2mm2, adj f117,f118,f119,f121
  f312: plane 22x10mm, normal (0.41,-0.91,0), area 190.2mm2, adj f51,f52,f53,f115,f122
  f313: bspline ~20.61x18.22mm, area 300.7mm2, adj f50,f55,f57,f115,f117
PLACE A rot(axis=(0.91,-0.34,-0.23),72.2deg) t=(-27.86,-95.42,-9.7)mm
PLACE B at identity fixed
MATE fastened A.f7 <-> B.f146  axis (0.47,0.81,-0.34) through (-24.58,-85.63,-2.36)mm
